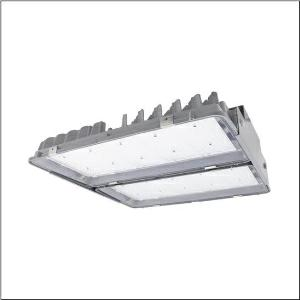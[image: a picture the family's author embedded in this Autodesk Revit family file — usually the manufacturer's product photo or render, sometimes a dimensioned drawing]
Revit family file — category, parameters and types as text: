
# Revit family: highbay_11xtreme_51hf81db4wma
name_source: partatom
category: Lighting Fixtures
units: mm (PartAtom-declared; Revit-internal decimal feet)

## family parameters
Cut with Voids When Loaded = No
Host = Face
Light Source = No
Part Type = Normal
Room Calculation Point = No
Round Connector Dimension = Use Diameter
Shared = No

## types (1)
- --- (1 x LED, 76000 lm, 422.2 W, 4000K)
    Apparent Load = 422 VA
    CIE Flux Codes = 88 96 99 100 100
    Color Rendering = 80
    Color Temperature = 4000K
    Default Elevation = 1800 mm
    Description = Highbay 11Xtreme, LED high bay luminaire, primary light control with lens, of PMMA, primary optical cover: cover, of toughened safety glass, light emission: direct distribution, primary light characteristic: symmetric, installation type: suspended mounting, surface-mounted, 2x LED module,for 1x 2x LED, rated luminous flux: 76.000lm, luminous efficacy: 180lm/W, light colour: 840, colour temperature: 4000K, with cable H07RN-F 5x 1.5mm², mains connection: 220..240V, AC, 50/60Hz, cable length: 1,5m, rated input power: 422W, luminaire housing, of diecast aluminium, partly coated, silver, length: 595mm, width: 560mm, height: 195mm, protection rating (complete): IP66, insulation class (complete): insulation class I (protective earthing), certification: CE, ENEC, UKCA, protection symbol: D, ball protection: ball impact resistant according to DIN VDE 0710 part 13 (with chain suspension), impact resistance: IK08, permissible operating ambient temperature: -25..+45°C, reducing of maximum allowable ambient temperature of 5°C with ceiling mounting, packaging unit: 1 piece
    Height = 157 mm
    Lamp = 1 x LED
    Lamp Light Flux = 76000 lm
    Lamp Power = 422.2 W
    Lamp count = 1
    Length = 593 mm
    Luminous efficacy = 180 lm/W
    Manufacturer = Siteco
    ModVariant = No
    Model = 51HF81DB4WMA
    Mounting Place = Ceiling
    Mounting Type = Pendant
    Number of Poles = 1
    OnlyDefault = Yes
    Power Factor = 1
    Product Name = Highbay 11Xtreme
    Product group = LED high bay luminaire
    ProductGroupID = 903
    Protection Class = Protection class I
    Protection Degree = IP 66
    RLX_Detail_Level = 1
    RLX_Emergency_Light_Flux = 0 lm
    RLX_Emergency_Type = 0
    RLX_Emergency_Type_DB = No
    RlxData = <blob elided: 33857 chars, md5=6ba8a686>
    Socket = socket
    Standby Power = 0 W
    System Light Flux = 76000 lm
    System Power = 422 W
    Type Comments = factory setting: luminous flux: 100 % | dim-lin: 254 | 1389 mA
    Type Image = l_1258340.jpg
    URL = http://relux.com
    VarID = @adj_052977
    Voltage = 0 V
    Weight = 0.00 kg
    Width = 278 mm

## geometry (parser evidence)
native form markers: Blend x4, Sweep x10
no freeform markers — native parametric forms only
